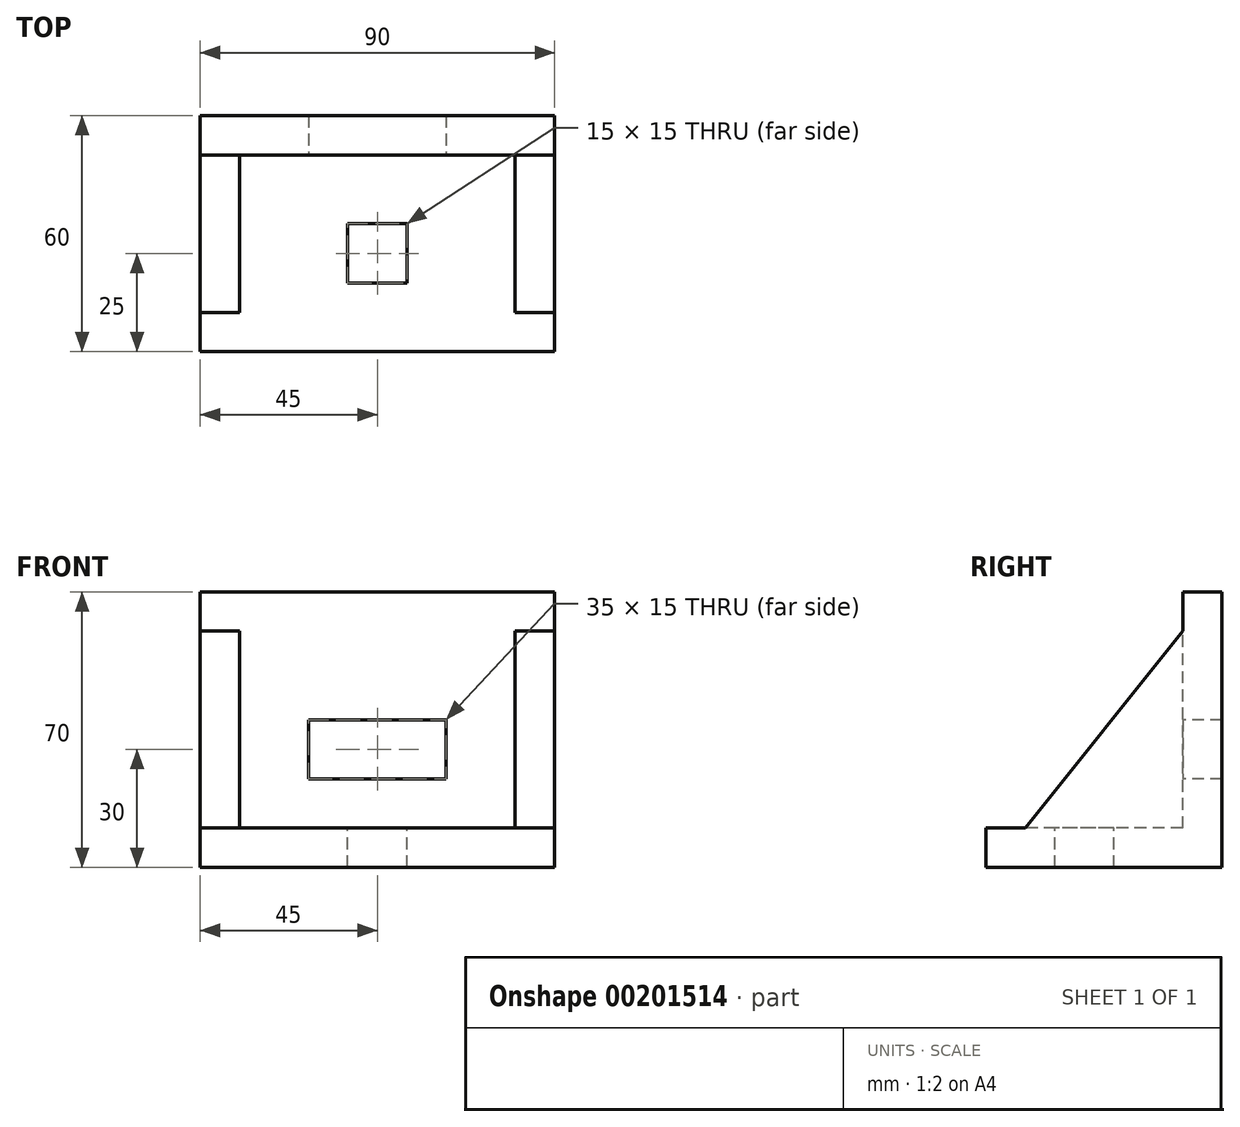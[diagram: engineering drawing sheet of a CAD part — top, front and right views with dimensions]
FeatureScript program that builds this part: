
annotation { "Feature Type Name" : "Feature", "Feature Type Description" : "" }
export const myFeature = defineFeature(function(context is Context, id is Id, definition is map)
    precondition{}
    {
        {
            var Q0;
            Q0=qCreatedBy(makeId("Top.planeOp"),FACE);
            var sketch = newSketch(context, id + "F0", { "sketchPlane" : qUnion([Q0])});
            skLineSegment(sketch, "E0.bottom", {"start": v(-45, 0) * mm, "end": v(0, 0) * mm});
            skLineSegment(sketch, "E0.top", {"start": v(-45, -60) * mm, "end": v(0, -60) * mm});
            skLineSegment(sketch, "E0.left", {"start": v(-45, 0) * mm, "end": v(-45, -60) * mm});
            skLineSegment(sketch, "E1.top", {"start": v(-45, -10) * mm, "end": v(0, -10) * mm});
            skLineSegment(sketch, "E1.left", {"start": v(-45, 0) * mm, "end": v(-45, -10) * mm});
            skLineSegment(sketch, "E2.bottom", {"start": v(-45, 0) * mm, "end": v(-35, 0) * mm});
            skLineSegment(sketch, "E2.top", {"start": v(-45, -50) * mm, "end": v(-35, -50) * mm});
            skLineSegment(sketch, "E2.left", {"start": v(-45, 0) * mm, "end": v(-45, -50) * mm});
            skLineSegment(sketch, "E2.right", {"start": v(-35, 0) * mm, "end": v(-35, -50) * mm});
            skLineSegment(sketch, "E3.bottom", {"start": v(0, 20.73) * mm, "end": v(0, 20.73) * mm});
            skLineSegment(sketch, "E3.top", {"start": v(0, -76.58) * mm, "end": v(0, -76.58) * mm});
            skLineSegment(sketch, "E3.left", {"start": v(0, 20.73) * mm, "end": v(0, -76.58) * mm});
            skLineSegment(sketch, "E3.right", {"start": v(0, 20.73) * mm, "end": v(0, -76.58) * mm, "construction": true});
            skLineSegment(sketch, "E4", {"start": v(0, -27.5) * mm, "end": v(-7.5, -27.5) * mm});
            skLineSegment(sketch, "E5", {"start": v(-7.5, -27.5) * mm, "end": v(-7.5, -42.5) * mm});
            skLineSegment(sketch, "E6", {"start": v(-7.5, -42.5) * mm, "end": v(0, -42.5) * mm});
            skSolve(sketch);
        }
        {
            var Q0;
            {var subQ7=sQuery(id+"F0.wireOp",EDGE,"E0.top");Q0=makeQuery(id+"F0.imprint","IMPRINT",FACE,{"disambiguationData":[TD([[makeQuery(id+"F0.imprint","IMPRINT",EDGE,{"derivedFrom":subQ7}),1.0]])]});}
            var Q1;
            {var subQ5=sQuery(id+"F0.wireOp",EDGE,"E2.top");Q1=makeQuery(id+"F0.imprint","IMPRINT",FACE,{"disambiguationData":[TD([[makeQuery(id+"F0.imprint","IMPRINT",EDGE,{"derivedFrom":subQ5}),1.0]])]});}
            var Q2;
            {var subQ5=sQuery(id+"F0.wireOp",EDGE,"E2.bottom");Q2=makeQuery(id+"F0.imprint","IMPRINT",FACE,{"disambiguationData":[TD([[makeQuery(id+"F0.imprint","IMPRINT",EDGE,{"derivedFrom":subQ5}),-1.0]])]});}
            var Q3;
            {var subQ0=sQuery(id+"F0.wireOp",EDGE,"E0.bottom");Q3=makeQuery(id+"F0.imprint","IMPRINT",FACE,{"disambiguationData":[TD([[makeQuery(id+"F0.imprint","IMPRINT",EDGE,{"derivedFrom":subQ0}),-1.0]])]});}
            extrude(context, id + "F1", {"entities" : qUnion([Q0, Q1, Q2, Q3]), "oppositeDirection" : true, "depth" : 10 * mm});
        }
        {
            var Q0;
            {var subQ5=sQuery(id+"F0.wireOp",EDGE,"E2.bottom");Q0=makeQuery(id+"F0.imprint","IMPRINT",FACE,{"disambiguationData":[TD([[makeQuery(id+"F0.imprint","IMPRINT",EDGE,{"derivedFrom":subQ5}),-1.0]])]});}
            var Q1;
            {var subQ0=sQuery(id+"F0.wireOp",EDGE,"E0.bottom");Q1=makeQuery(id+"F0.imprint","IMPRINT",FACE,{"disambiguationData":[TD([[makeQuery(id+"F0.imprint","IMPRINT",EDGE,{"derivedFrom":subQ0}),-1.0]])]});}
            extrude(context, id + "F2", {"entities" : qUnion([Q0, Q1]), "operationType" : NewBodyOperationType.ADD, "depth" : 60 * mm});
        }
        {
            var Q0;
            Q0=qCreatedBy(makeId("Top.planeOp"),FACE);
            cPlane(context, id + "F3", {"entities" : qUnion([Q0]), "cplaneType" : CPlaneType.OFFSET, "offset" : 50 * mm, "width" : 150 * mm, "height" : 150 * mm});
        }
        {
            var Q0;
            Q0=qCreatedBy(id+"F3.planeOp",FACE);
            var sketch = newSketch(context, id + "F4", { "sketchPlane" : qUnion([Q0])});
            skLineSegment(sketch, "E7.0", {"start": v(-35, 0) * mm, "end": v(-35, -10) * mm});
            skLineSegment(sketch, "E7.1", {"start": v(-45, -10) * mm, "end": v(-35, -10) * mm});
            skLineSegment(sketch, "E7.2", {"start": v(-45, 0) * mm, "end": v(-45, -10) * mm});
            skLineSegment(sketch, "E7.3", {"start": v(-45, 0) * mm, "end": v(-35, 0) * mm});
            skPoint(sketch, "E8.orphan", {"position": v(0, -10) * mm});
            skPoint(sketch, "E9.orphan", {"position": v(-35, -50) * mm});
            skPoint(sketch, "E10.orphan", {"position": v(-45, -50) * mm});
            skSolve(sketch);
        }
        {
            var Q1;
            {var subQ5=sQuery(id+"F0.wireOp",EDGE,"E2.top");Q1=makeQuery(id+"F0.imprint","IMPRINT",FACE,{"disambiguationData":[TD([[makeQuery(id+"F0.imprint","IMPRINT",EDGE,{"derivedFrom":subQ5}),1.0]])]});}
            var Q2;
            Q2=makeQuery(id+"F4.imprint","IMPRINT",FACE,{"disambiguationData":[TD([[makeQuery(id+"F4.imprint","IMPRINT",EDGE,{"derivedFrom":sQuery(id+"F4.wireOp",EDGE,"E7.0")}),-1.0]])]});
            loft(context, id + "F5", {"operationType" : NewBodyOperationType.ADD, "sheetProfilesArray" : [{ "sheetProfileEntities" : qUnion([Q1]) }, { "sheetProfileEntities" : qUnion([Q2]) }]});
        }
        {
            var Q0;
            Q0=makeQuery(id+"F2.opExtrude","SWEPT_FACE",FACE,{"disambiguationData":[OSD([sQuery(id+"F0.wireOp",EDGE,"E1.top")])]});
            var sketch = newSketch(context, id + "F6", { "sketchPlane" : qUnion([Q0])});
            skLineSegment(sketch, "E11", {"start": v(0, 27.5) * mm, "end": v(-17.5, 27.5) * mm});
            skLineSegment(sketch, "E12", {"start": v(-17.5, 27.5) * mm, "end": v(-17.5, 12.5) * mm});
            skLineSegment(sketch, "E13", {"start": v(-17.5, 12.5) * mm, "end": v(0, 12.5) * mm});
            skLineSegment(sketch, "E14", {"start": v(0, 12.5) * mm, "end": v(0, 27.5) * mm});
            skLineSegment(sketch, "E15", {"start": v(-21.37, 20) * mm, "end": v(5.7, 20) * mm, "construction": true});
            skPoint(sketch, "E15.startSnap0", {"position": v(-17.5, 20) * mm});
            skPoint(sketch, "E15.endSnap0", {"position": v(0, 20) * mm});
            skSolve(sketch);
        }
        {
            var Q0;
            Q0=qSketchRegion(id+"F6",true);
            extrude(context, id + "F7", {"entities" : qUnion([Q0]), "operationType" : NewBodyOperationType.REMOVE, "oppositeDirection" : true, "depth" : 25 * mm});
        }
        {
            var Q0;
            Q0=makeQuery(id+"F1.opExtrude","SWEPT_BODY",BODY,{"disambiguationData":[OSD([sQuery(id+"F0.wireOp",EDGE,"E0.top"),sQuery(id+"F0.wireOp",EDGE,"E0.left"),sQuery(id+"F0.wireOp",EDGE,"E0.bottom"),sQuery(id+"F0.wireOp",EDGE,"E2.bottom"),sQuery(id+"F0.wireOp",EDGE,"E2.left"),sQuery(id+"F0.wireOp",EDGE,"E3.left"),sQuery(id+"F0.wireOp",EDGE,"E4"),sQuery(id+"F0.wireOp",EDGE,"E5"),sQuery(id+"F0.wireOp",EDGE,"E6")])]});
            var Q1;
            Q1=qCreatedBy(makeId("Right.planeOp"),FACE);
            mirror(context, id + "F8", {"operationType" : NewBodyOperationType.ADD, "entities" : qUnion([Q0]), "mirrorPlane" : qUnion([Q1])});
        }
    });
